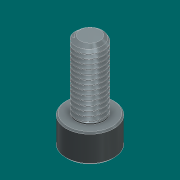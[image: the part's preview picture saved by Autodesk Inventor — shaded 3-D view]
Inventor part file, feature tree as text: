
AUTODESK INVENTOR PART (.ipt)
format: ipt  version: 2016 SP1 (Build 200210100, 210)  size: 548,352 bytes
history: native  units: mm
features: revolve x1
ambient origin geometry x8: Origin, YZ Plane, XZ Plane, XY Plane, X Axis, Y Axis, Z Axis, Center Point
bodies: Solid1 (feature_tree)
feature tree (1):
  revolve  "Revolve1"  [1 undecoded]
note: 1 required parameter value undecoded (feature->parameter linkage not recoverable at this tier; creation-order binding heuristic only, values carry confidence <= 0.55)
